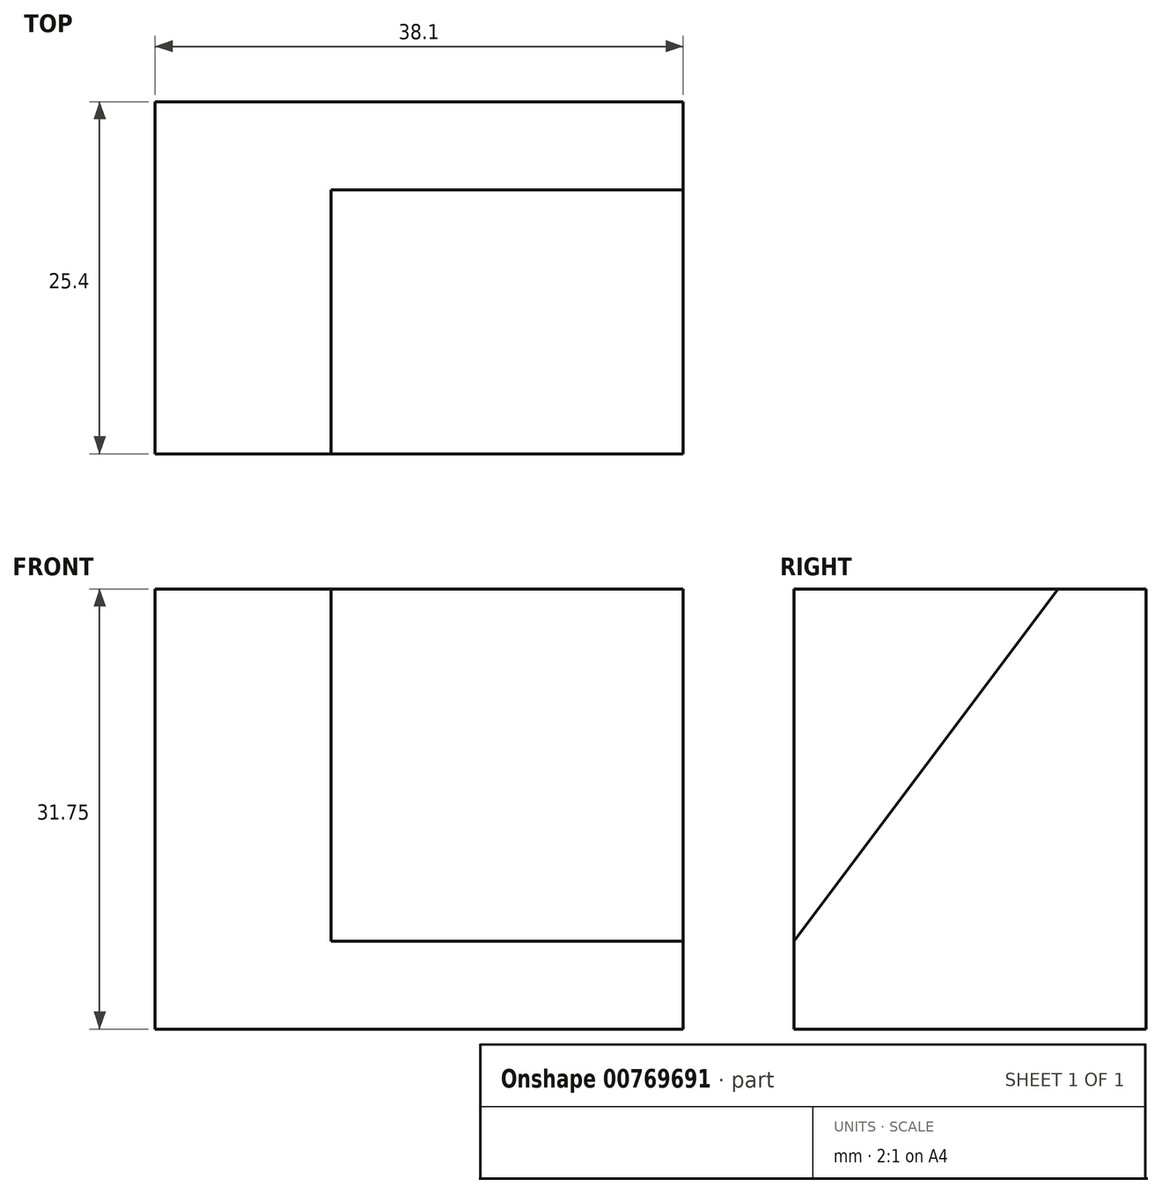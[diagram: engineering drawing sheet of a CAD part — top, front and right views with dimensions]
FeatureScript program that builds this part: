
annotation { "Feature Type Name" : "Feature", "Feature Type Description" : "" }
export const myFeature = defineFeature(function(context is Context, id is Id, definition is map)
    precondition{}
    {
        {
            var Q0;
            Q0=qCreatedBy(makeId("Right.planeOp"),FACE);
            var sketch = newSketch(context, id + "F0", { "sketchPlane" : qUnion([Q0])});
            skLineSegment(sketch, "E0", {"start": v(0, 0) * mm, "end": v(25.4, 0) * mm});
            skLineSegment(sketch, "E1", {"start": v(25.4, 0) * mm, "end": v(25.4, 31.75) * mm});
            skLineSegment(sketch, "E2", {"start": v(25.4, 31.75) * mm, "end": v(0, 31.75) * mm});
            skLineSegment(sketch, "E3", {"start": v(0, 31.75) * mm, "end": v(0, 0) * mm});
            skLineSegment(sketch, "E4", {"start": v(0, 31.75) * mm, "end": v(0, 31.75) * mm});
            skSolve(sketch);
        }
        {
            var Q0;
            Q0 = qSketchRegion(id + "F0", true);
            extrude(context, id + "F1", {"entities" : qUnion([Q0]), "depth" : 38.1 * mm, "offsetDistance" : 25.4 * mm});
        }
        {
            var Q0;
            Q0=makeQuery(id+"F1.opExtrude","CAP_FACE",FACE,{"disambiguationData":[OSD([sQuery(id+"F0.wireOp",EDGE,"E0"),sQuery(id+"F0.wireOp",EDGE,"E1"),sQuery(id+"F0.wireOp",EDGE,"E2"),sQuery(id+"F0.wireOp",EDGE,"E3")])],"isStart":false});
            var sketch = newSketch(context, id + "F2", { "sketchPlane" : qUnion([Q0])});
            skLineSegment(sketch, "E5", {"start": v(0, 0) * mm, "end": v(0, 6.35) * mm});
            skLineSegment(sketch, "E6", {"start": v(25.4, 31.75) * mm, "end": v(19.05, 31.75) * mm});
            skLineSegment(sketch, "E7", {"start": v(19.05, 31.75) * mm, "end": v(0, 6.35) * mm});
            skLineSegment(sketch, "E8", {"start": v(0, 0) * mm, "end": v(25.4, 0) * mm});
            skLineSegment(sketch, "E9", {"start": v(25.4, 0) * mm, "end": v(25.4, 31.75) * mm});
            skSolve(sketch);
        }
        {
            var Q0;
            {var subQ0=sQuery(id+"F2.wireOp",EDGE,"E7");Q0=makeQuery(id+"F2.imprint","IMPRINT",FACE,{"disambiguationData":[TD([[makeQuery(id+"F2.imprint","IMPRINT",EDGE,{"derivedFrom":subQ0}),-1.0]])]});}
            extrude(context, id + "F3", {"entities" : qUnion([Q0]), "operationType" : NewBodyOperationType.REMOVE, "oppositeDirection" : true, "depth" : 25.4 * mm, "offsetDistance" : 25.4 * mm});
        }
    });
